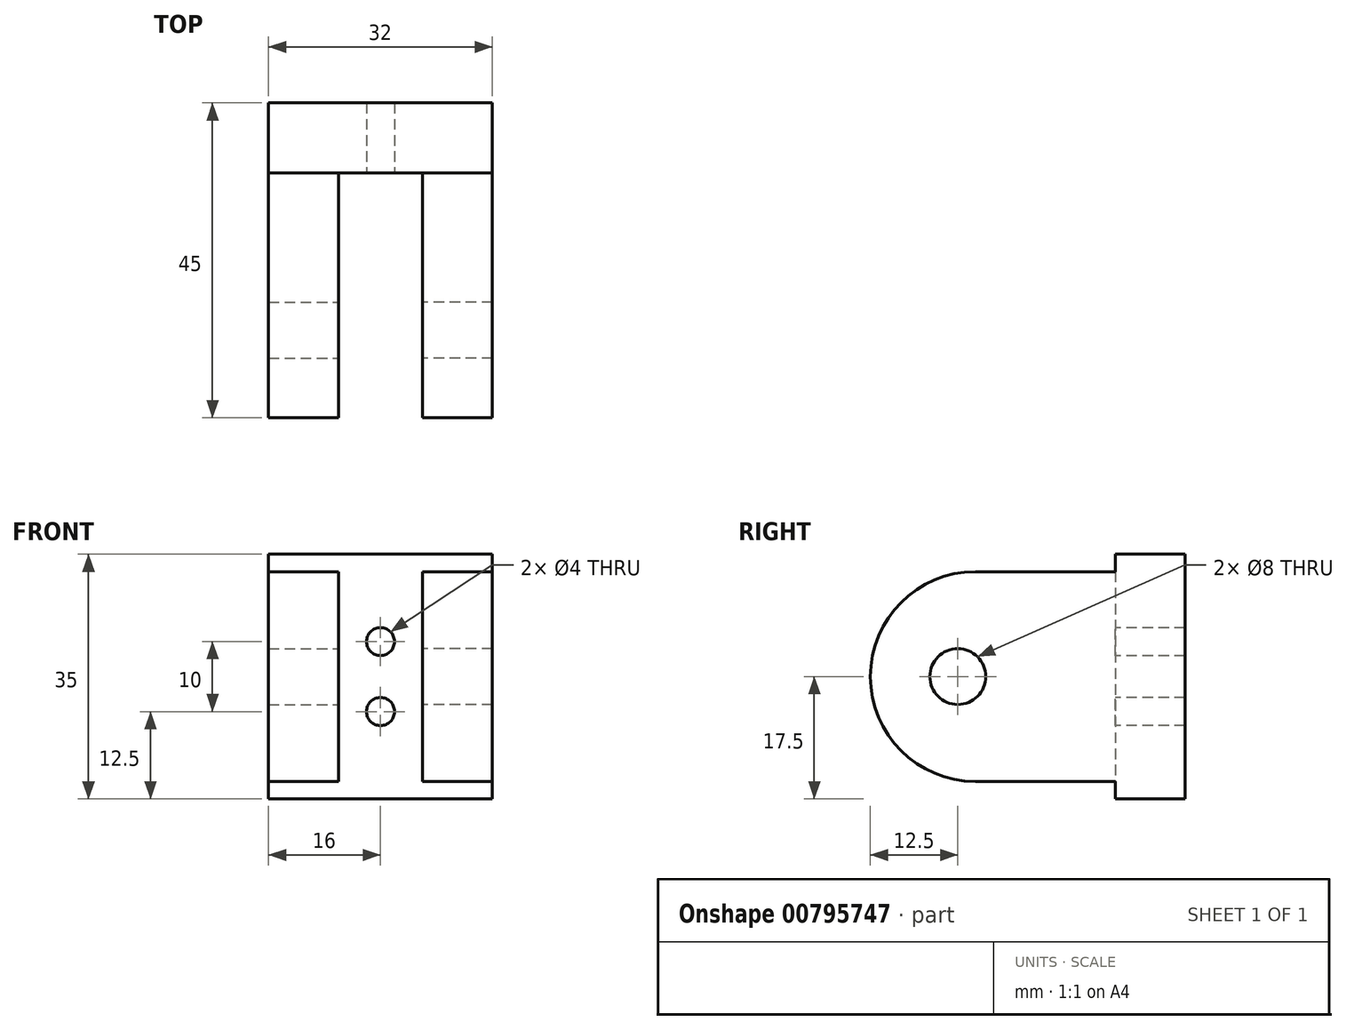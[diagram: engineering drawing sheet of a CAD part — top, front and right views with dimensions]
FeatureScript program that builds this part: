
annotation { "Feature Type Name" : "Feature", "Feature Type Description" : "" }
export const myFeature = defineFeature(function(context is Context, id is Id, definition is map)
    precondition{}
    {
        {
            var Q0;
            Q0=qCreatedBy(makeId("Front.planeOp"),FACE);
            var sketch = newSketch(context, id + "F0", { "sketchPlane" : qUnion([Q0])});
            skLineSegment(sketch, "E0.bottom", {"start": v(-16, -17.5) * mm, "end": v(16, -17.5) * mm});
            skLineSegment(sketch, "E0.top", {"start": v(-16, 17.5) * mm, "end": v(16, 17.5) * mm});
            skLineSegment(sketch, "E0.left", {"start": v(-16, -17.5) * mm, "end": v(-16, 17.5) * mm});
            skLineSegment(sketch, "E0.right", {"start": v(16, -17.5) * mm, "end": v(16, 17.5) * mm});
            skPoint(sketch, "E0.middle", {"position": v(0, 0) * mm});
            skSolve(sketch);
        }
        {
            var Q0;
            Q0 = qSketchRegion(id + "F0", true);
            extrude(context, id + "F1", {"entities" : qUnion([Q0]), "depth" : 10 * mm, "offsetDistance" : 25 * mm});
        }
        {
            var Q0;
            Q0=makeQuery(id+"F1.opExtrude","CAP_FACE",FACE,{"disambiguationData":[OSD([sQuery(id+"F0.wireOp",EDGE,"E0.bottom"),sQuery(id+"F0.wireOp",EDGE,"E0.top"),sQuery(id+"F0.wireOp",EDGE,"E0.left"),sQuery(id+"F0.wireOp",EDGE,"E0.right")])],"isStart":false});
            var sketch = newSketch(context, id + "F2", { "sketchPlane" : qUnion([Q0])});
            skLineSegment(sketch, "E1", {"start": v(-6, 17.5) * mm, "end": v(-6, -17.5) * mm});
            skLineSegment(sketch, "E2", {"start": v(6, 17.5) * mm, "end": v(6, -17.5) * mm, "construction": true});
            skLineSegment(sketch, "E3", {"start": v(-16, 15) * mm, "end": v(16, 15) * mm, "construction": true});
            skLineSegment(sketch, "E4.bottom", {"start": v(-6, 15) * mm, "end": v(-16, 15) * mm});
            skLineSegment(sketch, "E4.top", {"start": v(-6, -15) * mm, "end": v(-16, -15) * mm});
            skLineSegment(sketch, "E4.left", {"start": v(-6, 15) * mm, "end": v(-6, -15) * mm});
            skLineSegment(sketch, "E4.right", {"start": v(-16, 15) * mm, "end": v(-16, -15) * mm});
            skLineSegment(sketch, "E5.MirrorCS", {"start": v(6, 15) * mm, "end": v(6, -15) * mm});
            skLineSegment(sketch, "E6.MirrorCS", {"start": v(16, 15) * mm, "end": v(-16, 15) * mm, "construction": true});
            skLineSegment(sketch, "E7.MirrorCS", {"start": v(6, -15) * mm, "end": v(16, -15) * mm});
            skLineSegment(sketch, "E8", {"start": v(6, 15) * mm, "end": v(16, 15) * mm});
            skLineSegment(sketch, "E9", {"start": v(16, 15) * mm, "end": v(16, -15) * mm});
            skSolve(sketch);
        }
        {
            var Q0;
            {var subQ0=sQuery(id+"F2.wireOp",EDGE,"E4.bottom");Q0=makeQuery(id+"F2.imprint","IMPRINT",FACE,{"disambiguationData":[TD([[makeQuery(id+"F2.imprint","IMPRINT",EDGE,{"derivedFrom":subQ0}),1.0]])]});}
            var Q1;
            Q1=makeQuery(id+"F2.imprint","IMPRINT",FACE,{"disambiguationData":[TD([[makeQuery(id+"F2.imprint","IMPRINT",EDGE,{"derivedFrom":sQuery(id+"F2.wireOp",EDGE,"E5.MirrorCS")}),1.0]])]});
            extrude(context, id + "F3", {"entities" : qUnion([Q0, Q1]), "operationType" : NewBodyOperationType.ADD, "depth" : 35 * mm, "offsetDistance" : 25 * mm});
        }
        {
            var Q0;
            Q0=makeQuery(id+"F3.opExtrude","SWEPT_FACE",FACE,{"disambiguationData":[OSD([sQuery(id+"F2.wireOp",EDGE,"E1")])]});
            var sketch = newSketch(context, id + "F4", { "sketchPlane" : qUnion([Q0])});
            skCircle(sketch, "E10", {"center": v(-32.5, 0) * mm, "radius": 4 * mm});
            skPoint(sketch, "E10.centerSnap0", {"position": v(-45, 0) * mm});
            skSolve(sketch);
        }
        {
            var Q0;
            Q0=makeQuery(id+"F4.imprint","IMPRINT",FACE,{"disambiguationData":[TD([[makeQuery(id+"F4.imprint","IMPRINT",EDGE,{"derivedFrom":sQuery(id+"F4.wireOp",EDGE,"E10")}),1.0]])]});
            extrude(context, id + "F5", {"entities" : qUnion([Q0]), "operationType" : NewBodyOperationType.REMOVE, "endBound" : BoundingType.THROUGH_ALL, "oppositeDirection" : true, "depth" : 25 * mm, "offsetDistance" : 25 * mm});
        }
        {
            var Q0;
            Q0=makeQuery(id+"F3.opExtrude","SWEPT_FACE",FACE,{"disambiguationData":[OSD([sQuery(id+"F2.wireOp",EDGE,"E5.MirrorCS")])]});
            var sketch = newSketch(context, id + "F6", { "sketchPlane" : qUnion([Q0])});
            skCircle(sketch, "E11", {"center": v(32.5, 0) * mm, "radius": 4 * mm});
            skPoint(sketch, "E11.centerSnap0", {"position": v(45, 0) * mm});
            skSolve(sketch);
        }
        {
            var Q0;
            Q0=makeQuery(id+"F6.imprint","IMPRINT",FACE,{"disambiguationData":[TD([[makeQuery(id+"F6.imprint","IMPRINT",EDGE,{"derivedFrom":sQuery(id+"F6.wireOp",EDGE,"E11")}),1.0]])]});
            extrude(context, id + "F7", {"entities" : qUnion([Q0]), "operationType" : NewBodyOperationType.REMOVE, "endBound" : BoundingType.THROUGH_ALL, "oppositeDirection" : true, "depth" : 25 * mm, "offsetDistance" : 25 * mm});
        }
        {
            var Q0;
            Q0=makeQuery(id+"F3.opExtrude","CAP_EDGE",EDGE,{"disambiguationData":[OSD([sQuery(id+"F2.wireOp",EDGE,"E4.top")])],"isStart":false});
            var Q1;
            Q1=makeQuery(id+"F3.opExtrude","CAP_EDGE",EDGE,{"disambiguationData":[OSD([sQuery(id+"F2.wireOp",EDGE,"E7.MirrorCS")])],"isStart":false});
            var Q2;
            Q2=makeQuery(id+"F3.opExtrude","CAP_EDGE",EDGE,{"disambiguationData":[OSD([sQuery(id+"F2.wireOp",EDGE,"E4.bottom")])],"isStart":false});
            var Q3;
            Q3=makeQuery(id+"F3.opExtrude","CAP_EDGE",EDGE,{"disambiguationData":[OSD([sQuery(id+"F2.wireOp",EDGE,"E8")])],"isStart":false});
            fillet(context, id + "F8", {"entities" : qUnion([Q0, Q1, Q2, Q3]), "radius" : 15 * mm, "tangentPropagation" : true, "allowEdgeOverflow" : false});
        }
        {
            var Q0;
            Q0=makeQuery(id+"F1.opExtrude","CAP_FACE",FACE,{"disambiguationData":[OSD([sQuery(id+"F0.wireOp",EDGE,"E0.bottom"),sQuery(id+"F0.wireOp",EDGE,"E0.top"),sQuery(id+"F0.wireOp",EDGE,"E0.left"),sQuery(id+"F0.wireOp",EDGE,"E0.right")])],"isStart":false});
            var sketch = newSketch(context, id + "F9", { "sketchPlane" : qUnion([Q0])});
            skCircle(sketch, "E12", {"center": v(0, 5) * mm, "radius": 2 * mm});
            skPoint(sketch, "E12.centerSnap0", {"position": v(0, 17.5) * mm});
            skCircle(sketch, "E13", {"center": v(0, -5) * mm, "radius": 2 * mm});
            skPoint(sketch, "E13.centerSnap0", {"position": v(0, -17.5) * mm});
            skSolve(sketch);
        }
        {
            var Q0;
            Q0=makeQuery(id+"F9.imprint","IMPRINT",FACE,{"disambiguationData":[TD([[makeQuery(id+"F9.imprint","IMPRINT",EDGE,{"derivedFrom":sQuery(id+"F9.wireOp",EDGE,"E12")}),1.0]])]});
            var Q1;
            Q1=makeQuery(id+"F9.imprint","IMPRINT",FACE,{"disambiguationData":[TD([[makeQuery(id+"F9.imprint","IMPRINT",EDGE,{"derivedFrom":sQuery(id+"F9.wireOp",EDGE,"E13")}),1.0]])]});
            extrude(context, id + "F10", {"entities" : qUnion([Q0, Q1]), "operationType" : NewBodyOperationType.REMOVE, "endBound" : BoundingType.THROUGH_ALL, "oppositeDirection" : true, "depth" : 25 * mm, "offsetDistance" : 25 * mm});
        }
    });
